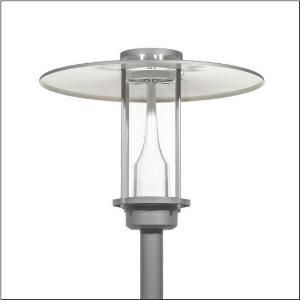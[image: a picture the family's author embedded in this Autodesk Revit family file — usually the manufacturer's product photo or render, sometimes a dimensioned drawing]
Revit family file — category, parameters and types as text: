
# Revit family: city-light_plus_iq___st1_2a_5xa5275kf14hp_140d
name_source: partatom
category: Lighting Fixtures
units: mm (PartAtom-declared; Revit-internal decimal feet)

## family parameters
Cut with Voids When Loaded = No
Host = Face
Light Source = No
Part Type = Normal
Room Calculation Point = No
Round Connector Dimension = Use Diameter
Shared = No

## types (1)
- --- (1 x LED, 4710 lm, 33.6 W, 4000K)
    Apparent Load = 34 VA
    CIE Flux Codes = 22 60 93 97 100
    Color Rendering = 70
    Color Temperature = 4000K
    Default Elevation = 1800 mm
    Description = City-Light Plus iQ, mast luminaire, Module 540 iQ-SR, primary light control with 3 zone facetted reflector, of plastic, silver coated, highly specular, structured, primary optical cover: cover, of PMMA, transparent, light distribution: ST1.2a, light emission: direct distribution, primary light characteristic: asymmetric, installation type: post-top, LED, High Power LED, rated luminous flux: 4.710lm, luminous efficacy: 140lm/W, light colour: 740, colour temperature: 4000K, control gear: ECG iQ, control: presetting dimming logarithmic, Street-Remote, Auto-Match, Temp-Guard, Lumen-Switch, Night-Set, Smart-Wire, Light-Fading, Desk-Remote (wireless, voltage-free reading and setting of iQ features in the workshop via application-optimized NFC function/RFID function), optimised constant luminous flux control (CLO 2.0), with terminal, 6-pole, max. 2.5mm², mains connection: 230..240V, AC, 50/60Hz, start of lifetime: 34W, end of service life: 36W, reduction: 15W, luminaire housing, upper part, of glass-fibre reinforced polyester, coated, Siteco® metallic grey (DB 702S), diameter: 750mm, height: 590mm, spigot size: d x l = 76 x 70mm (post-top) | with reducer (optional accessory) 60 x 70mm, post-top mast mounting element, of diecast aluminium, coated, Siteco® metallic grey (DB 702S), Module 540 iQ-SR, traffic white (RAL 9016), equipment: Power, protection rating (complete): IP65, insulation class (complete): insulation class II (safety insulation), certification: CE, ENEC, VDE, packaging unit: 1 piece

Light Distribution: ST1.2a
    Height = 590 mm
    Lamp = 1 x LED
    Lamp Light Flux = 4710 lm
    Lamp Power = 33.6 W
    Lamp count = 1
    Length = 750 mm
    Luminous efficacy = 140 lm/W
    Manufacturer = Siteco
    ModVariant = No
    Model = 5XA5275KF14HP
    Number of Poles = 1
    OnlyDefault = Yes
    Power Factor = 1
    Product Name = City-Light Plus iQ | ST1.2a
    Product group = mast luminaire | pylon top
    ProductGroupID = 6100
    Protection Class = Protection class II
    Protection Degree = IP 65
    RLX_Detail_Level = 1
    RLX_Emergency_Light_Flux = 0 lm
    RLX_Emergency_Type = 0
    RLX_Emergency_Type_DB = No
    RlxData = <blob elided: 52489 chars, md5=78cc712b>
    Socket = socket
    Standby Power = 0 W
    System Light Flux = 4710 lm
    System Power = 34 W
    Type Comments = factory setting: luminous flux: 100 % | dim-lin: 254 | 695 mA
    Type Image = l_1006456.jpg
    URL = http://relux.com
    VarID = @adj_146455
    Voltage = 0 V
    Weight = 0.00 kg
    Width = 0 mm  [stored 0 ft]

note: [stored X ft] marks values corroborated as IEEE doubles in the binary element streams (Revit-internal decimal feet)

## geometry (parser evidence)
native form markers: Blend x4, Sweep x12
no freeform markers — native parametric forms only
